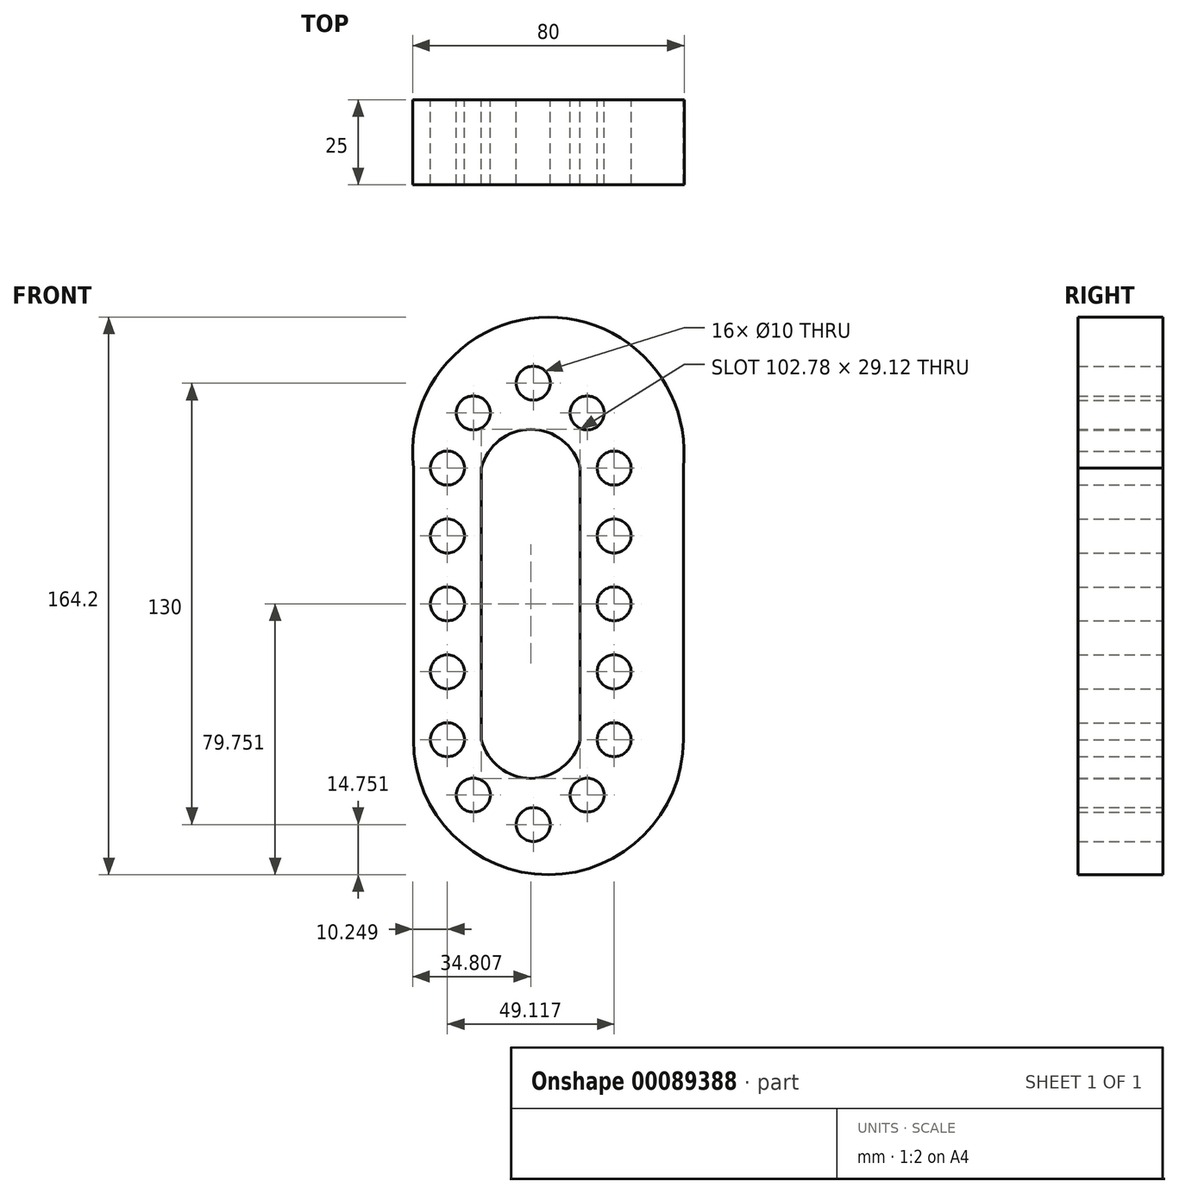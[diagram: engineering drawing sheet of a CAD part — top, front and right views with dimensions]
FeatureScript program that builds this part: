
annotation { "Feature Type Name" : "Feature", "Feature Type Description" : "" }
export const myFeature = defineFeature(function(context is Context, id is Id, definition is map)
    precondition{}
    {
        {
            var Q0;
            Q0=qCreatedBy(makeId("Front.planeOp"),FACE);
            var sketch = newSketch(context, id + "F0", { "sketchPlane" : qUnion([Q0])});
            skArc(sketch, "E0", {"start": v(13.82, 38.64) * mm, "mid": v(-0.74, 50.03) * mm, "end": v(-15.3, 38.64) * mm});
            skLineSegment(sketch, "E1", {"start": v(-15.3, 38.64) * mm, "end": v(-15.3, -41.36) * mm});
            skLineSegment(sketch, "E2", {"start": v(13.82, 38.64) * mm, "end": v(13.82, -41.36) * mm});
            skArc(sketch, "E3", {"start": v(-15.3, -41.36) * mm, "mid": v(-0.74, -52.75) * mm, "end": v(13.82, -41.36) * mm});
            skLineSegment(sketch, "E4", {"start": v(-35.3, 38.64) * mm, "end": v(-35.3, -41.36) * mm});
            skLineSegment(sketch, "E5", {"start": v(44.2, 38.64) * mm, "end": v(44.2, -41.36) * mm});
            skArc(sketch, "E6", {"start": v(44.2, 38.64) * mm, "mid": v(4.45, 83.09) * mm, "end": v(-35.3, 38.64) * mm});
            skArc(sketch, "E7", {"start": v(-35.3, -41.36) * mm, "mid": v(4.45, -81.11) * mm, "end": v(44.2, -41.36) * mm});
            skCircle(sketch, "E8", {"center": v(-25.3, -41.36) * mm, "radius": 5 * mm});
            skCircle(sketch, "E9", {"center": v(23.82, -41.36) * mm, "radius": 5 * mm});
            skPoint(sketch, "E9.perimeterSnap0", {"position": v(23.82, -41.36) * mm});
            skPoint(sketch, "E9.perimeterSnap1", {"position": v(0, -47.04) * mm});
            skCircle(sketch, "E10", {"center": v(0, 63.64) * mm, "radius": 5 * mm});
            skCircle(sketch, "E11", {"center": v(0, -66.36) * mm, "radius": 5 * mm});
            skCircle(sketch, "E12", {"center": v(-25.3, 38.64) * mm, "radius": 5 * mm});
            skCircle(sketch, "E13", {"center": v(23.82, 38.64) * mm, "radius": 5 * mm});
            skCircle(sketch, "E14", {"center": v(23.82, -1.36) * mm, "radius": 5 * mm});
            skCircle(sketch, "E15", {"center": v(-25.3, -1.36) * mm, "radius": 5 * mm});
            skCircle(sketch, "E16", {"center": v(-25.3, 18.64) * mm, "radius": 5 * mm});
            skCircle(sketch, "E17", {"center": v(23.82, 18.64) * mm, "radius": 5 * mm});
            skCircle(sketch, "E18", {"center": v(-25.3, -21.36) * mm, "radius": 5 * mm});
            skCircle(sketch, "E19", {"center": v(23.82, -21.36) * mm, "radius": 5 * mm});
            skCircle(sketch, "E20", {"center": v(15.87, 54.88) * mm, "radius": 5 * mm});
            skCircle(sketch, "E21", {"center": v(-17.66, 54.88) * mm, "radius": 5 * mm});
            skCircle(sketch, "E22", {"center": v(15.87, -57.66) * mm, "radius": 5 * mm});
            skCircle(sketch, "E23", {"center": v(-17.66, -57.66) * mm, "radius": 5 * mm});
            skSolve(sketch);
        }
        {
            var Q0;
            Q0=makeQuery(id+"F0.imprint","IMPRINT",FACE,{"disambiguationData":[TD([[makeQuery(id+"F0.imprint","IMPRINT",EDGE,{"derivedFrom":sQuery(id+"F0.wireOp",EDGE,"E0")}),-1.0]])]});
            extrude(context, id + "F1", {"entities" : qUnion([Q0]), "depth" : 25 * mm});
        }
    });
